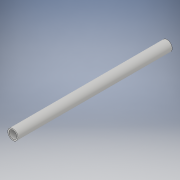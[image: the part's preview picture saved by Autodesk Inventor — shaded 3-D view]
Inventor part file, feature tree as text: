
AUTODESK INVENTOR PART (.ipt)
format: ipt  version: 2019 (Build 230136000, 136)  size: 97,280 bytes
history: native  units: in
note: dims shown in document units (in); Inventor stores cm internally (conversion verified against a paired STEP export)
features: extrude x2, sketch x2
ambient origin geometry x8: Origin, YZ Plane, XZ Plane, XY Plane, X Axis, Y Axis, Z Axis, Center Point
bodies: Solid1 (feature_tree)
feature tree (4):
  extrude  "Extrusion1"  Depth=15.0in TaperAngle=0.0deg
  extrude  "Extrusion2"  Depth=15.0in TaperAngle=0.0deg
  sketch  "Sketch1"  dims[d0=1.0in d1=15.0in d2=0.0in]
  sketch  "Sketch2"  dims[d3=0.12in d4=15.0in d5=0.0in]
